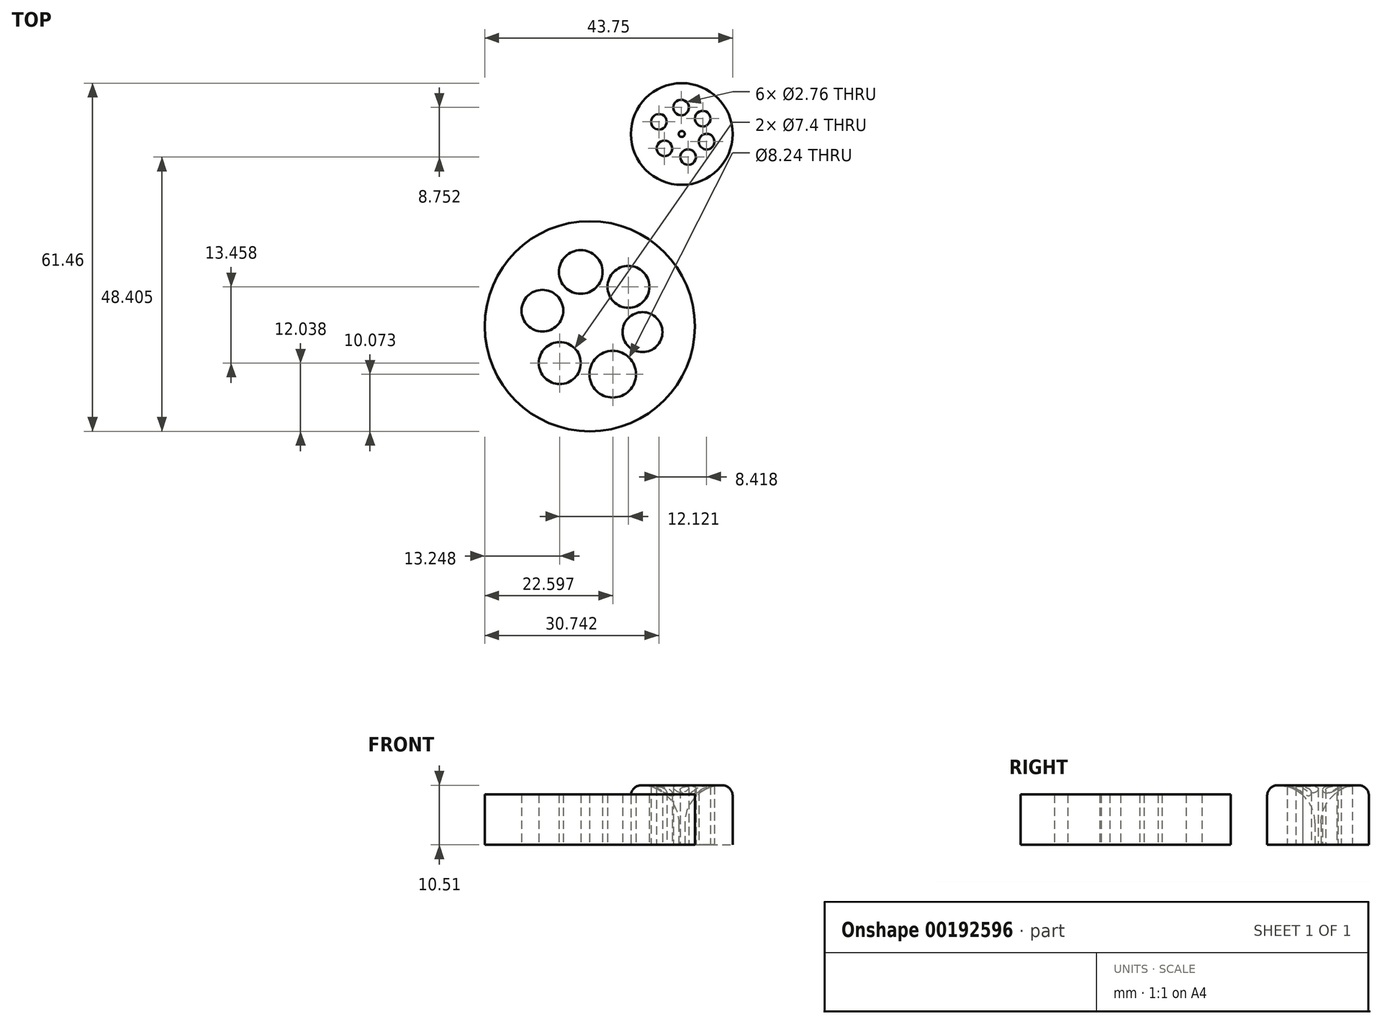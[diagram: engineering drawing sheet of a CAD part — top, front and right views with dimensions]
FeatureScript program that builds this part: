
annotation { "Feature Type Name" : "Feature", "Feature Type Description" : "" }
export const myFeature = defineFeature(function(context is Context, id is Id, definition is map)
    precondition{}
    {
        {
            var Q0;
            Q0=qCreatedBy(makeId("Top.planeOp"),FACE);
            var sketch = newSketch(context, id + "F0", { "sketchPlane" : qUnion([Q0])});
            skCircle(sketch, "E0", {"center": v(-15.73, 9.94) * mm, "radius": 8.97 * mm});
            skCircle(sketch, "E1", {"center": v(-19.76, 12.1) * mm, "radius": 1.38 * mm});
            skCircle(sketch, "E2", {"center": v(-18.78, 7.4) * mm, "radius": 1.38 * mm});
            skCircle(sketch, "E3", {"center": v(-14.6, 5.87) * mm, "radius": 1.38 * mm});
            skCircle(sketch, "E4", {"center": v(-11.34, 8.6) * mm, "radius": 1.38 * mm});
            skCircle(sketch, "E5", {"center": v(-12.03, 12.66) * mm, "radius": 1.38 * mm});
            skCircle(sketch, "E6", {"center": v(-15.83, 14.62) * mm, "radius": 1.38 * mm});
            skCircle(sketch, "E7", {"center": v(-15.73, 9.94) * mm, "radius": 0.53 * mm});
            skSolve(sketch);
        }
        {
            var Q0;
            Q0 = qSketchRegion(id + "F0", true);
            extrude(context, id + "F1", {"entities" : qUnion([Q0]), "depth" : 10.52 * mm});
        }
        {
            var Q0;
            Q0=makeQuery(id+"F1.opExtrude","CAP_EDGE",EDGE,{"disambiguationData":[OSD([sQuery(id+"F0.wireOp",EDGE,"E7")])],"isStart":false});
            fillet(context, id + "F2", {"entities" : qUnion([Q0]), "radius" : 6.68 * mm, "tangentPropagation" : true, "allowEdgeOverflow" : false});
        }
        {
            var Q0;
            Q0=makeQuery(id+"F1.opExtrude","CAP_EDGE",EDGE,{"disambiguationData":[OSD([sQuery(id+"F0.wireOp",EDGE,"E0")])],"isStart":false});
            fillet(context, id + "F3", {"entities" : qUnion([Q0]), "radius" : 1.84 * mm, "allowEdgeOverflow" : false});
        }
        {
            var Q0;
            Q0=qCreatedBy(makeId("Top.planeOp"),FACE);
            var sketch = newSketch(context, id + "F4", { "sketchPlane" : qUnion([Q0])});
            skCircle(sketch, "E8", {"center": v(-31.96, -24) * mm, "radius": 18.54 * mm});
            skCircle(sketch, "E9", {"center": v(-40.32, -21.25) * mm, "radius": 3.68 * mm});
            skCircle(sketch, "E10", {"center": v(-33.55, -14.42) * mm, "radius": 3.85 * mm});
            skCircle(sketch, "E11", {"center": v(-25.13, -17.04) * mm, "radius": 3.7 * mm});
            skCircle(sketch, "E12", {"center": v(-22.65, -25.03) * mm, "radius": 3.53 * mm});
            skCircle(sketch, "E13", {"center": v(-27.9, -32.47) * mm, "radius": 4.12 * mm});
            skCircle(sketch, "E14", {"center": v(-37.25, -30.5) * mm, "radius": 3.7 * mm});
            skSolve(sketch);
        }
        {
            var Q0;
            Q0=makeQuery(id+"F4.imprint","IMPRINT",FACE,{"disambiguationData":[TD([[makeQuery(id+"F4.imprint","IMPRINT",EDGE,{"derivedFrom":sQuery(id+"F4.wireOp",EDGE,"E8")}),1.0]])]});
            extrude(context, id + "F5", {"entities" : qUnion([Q0]), "depth" : 8.9 * mm});
        }
    });
